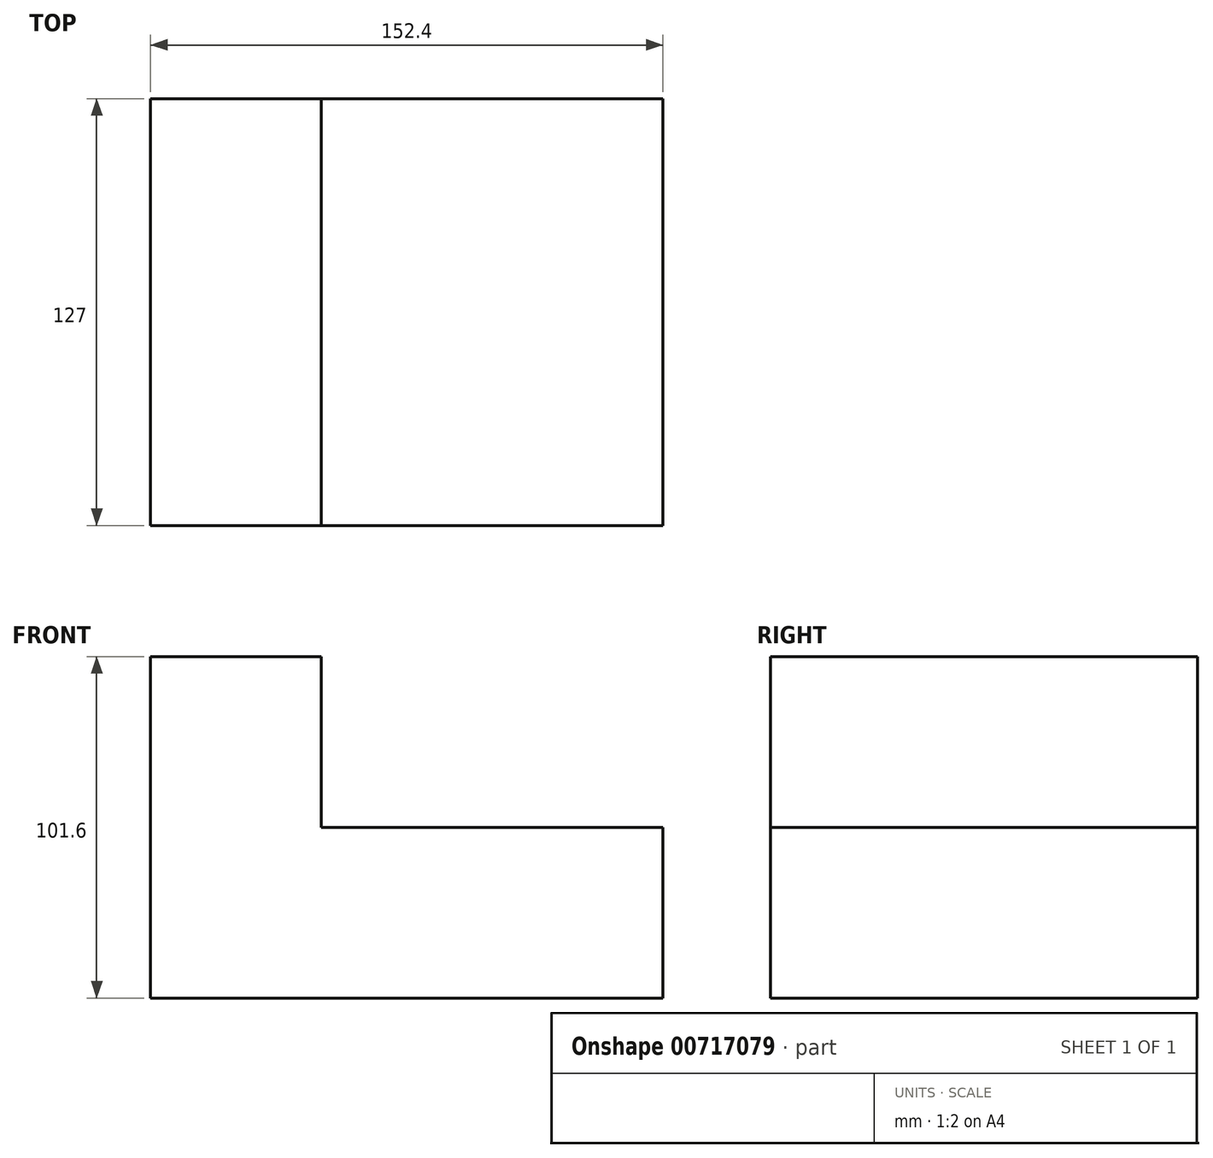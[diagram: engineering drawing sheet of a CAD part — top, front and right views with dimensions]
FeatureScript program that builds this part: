
annotation { "Feature Type Name" : "Feature", "Feature Type Description" : "" }
export const myFeature = defineFeature(function(context is Context, id is Id, definition is map)
    precondition{}
    {
        {
            var Q0;
            Q0=qCreatedBy(makeId("Front.planeOp"),FACE);
            var sketch = newSketch(context, id + "F0", { "sketchPlane" : qUnion([Q0])});
            skLineSegment(sketch, "E0", {"start": v(-131.9, -46.3) * mm, "end": v(20.5, -46.3) * mm});
            skLineSegment(sketch, "E1", {"start": v(20.5, -46.3) * mm, "end": v(20.5, 4.5) * mm});
            skLineSegment(sketch, "E2", {"start": v(20.5, 4.5) * mm, "end": v(-81.1, 4.5) * mm});
            skLineSegment(sketch, "E3", {"start": v(-81.1, 4.5) * mm, "end": v(-81.1, 55.3) * mm});
            skLineSegment(sketch, "E4", {"start": v(-81.1, 55.3) * mm, "end": v(-131.9, 55.3) * mm});
            skLineSegment(sketch, "E5", {"start": v(-131.9, 55.3) * mm, "end": v(-131.9, -46.3) * mm});
            skSolve(sketch);
        }
        {
            var Q0;
            Q0=makeQuery(id+"F0.imprint","IMPRINT",FACE,{"disambiguationData":[TD([[makeQuery(id+"F0.imprint","IMPRINT",EDGE,{"derivedFrom":sQuery(id+"F0.wireOp",EDGE,"E0")}),1.0]])]});
            extrude(context, id + "F1", {"entities" : qUnion([Q0]), "depth" : 127 * mm, "offsetDistance" : 25.4 * mm});
        }
    });
